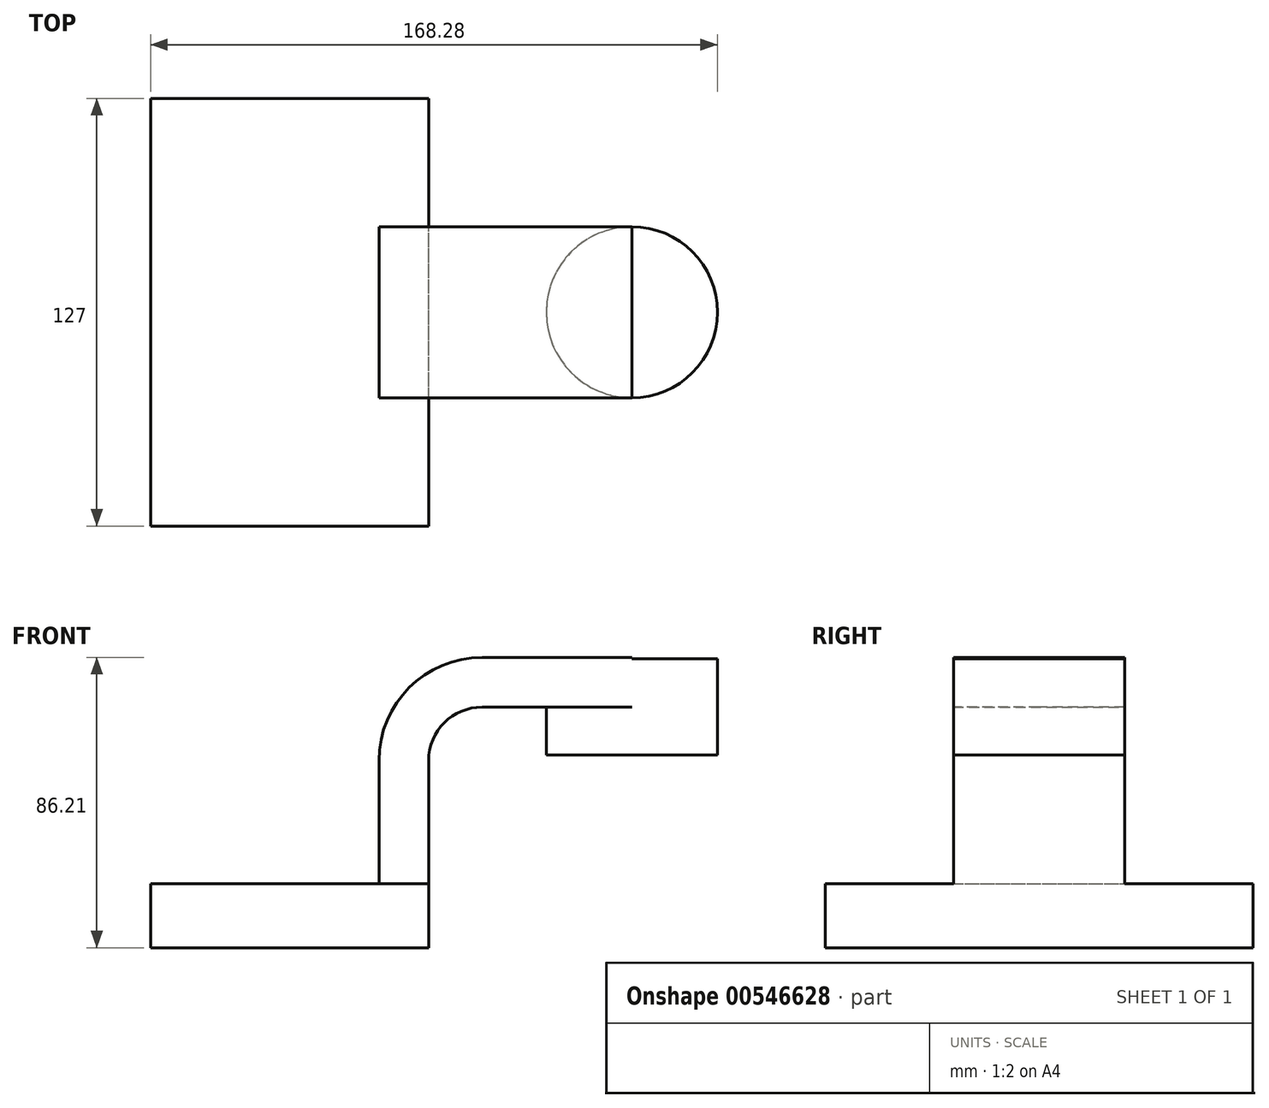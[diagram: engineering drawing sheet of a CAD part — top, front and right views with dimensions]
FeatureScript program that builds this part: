
annotation { "Feature Type Name" : "Feature", "Feature Type Description" : "" }
export const myFeature = defineFeature(function(context is Context, id is Id, definition is map)
    precondition{}
    {
        {
            var Q0;
            Q0=qCreatedBy(makeId("Front.planeOp"),FACE);
            var sketch = newSketch(context, id + "F0", { "sketchPlane" : qUnion([Q0])});
            skLineSegment(sketch, "E0.bottom", {"start": v(41.27, 9.53) * mm, "end": v(-41.28, 9.53) * mm});
            skLineSegment(sketch, "E0.top", {"start": v(41.28, -9.52) * mm, "end": v(-41.27, -9.53) * mm});
            skLineSegment(sketch, "E0.left", {"start": v(41.28, 9.53) * mm, "end": v(41.28, -9.52) * mm});
            skLineSegment(sketch, "E0.right", {"start": v(-41.28, 9.53) * mm, "end": v(-41.27, -9.52) * mm});
            skPoint(sketch, "E0.middle", {"position": v(0, 0) * mm});
            skLineSegment(sketch, "E1.bottom", {"start": v(76.2, 47.64) * mm, "end": v(76.2, 76.21) * mm});
            skLineSegment(sketch, "E1.top", {"start": v(127, 47.64) * mm, "end": v(127, 76.21) * mm});
            skLineSegment(sketch, "E1.left", {"start": v(76.2, 47.64) * mm, "end": v(127, 47.64) * mm});
            skLineSegment(sketch, "E1.right", {"start": v(76.2, 76.21) * mm, "end": v(127, 76.21) * mm});
            skPoint(sketch, "E1.middle", {"position": v(101.6, 61.93) * mm});
            skLineSegment(sketch, "E2", {"start": v(41.27, 9.53) * mm, "end": v(41.27, 46.05) * mm});
            skArc(sketch, "E3", {"start": v(41.27, 46.05) * mm, "mid": v(45.92, 57.28) * mm, "end": v(57.15, 61.93) * mm});
            skLineSegment(sketch, "E4", {"start": v(57.15, 61.93) * mm, "end": v(101.6, 61.93) * mm});
            skLineSegment(sketch, "E5.0", {"start": v(57.15, 76.68) * mm, "end": v(101.6, 76.68) * mm});
            skArc(sketch, "E5.1", {"start": v(26.52, 46.05) * mm, "mid": v(35.5, 67.7) * mm, "end": v(57.15, 76.68) * mm});
            skLineSegment(sketch, "E5.2", {"start": v(26.52, 9.53) * mm, "end": v(26.52, 46.05) * mm});
            skLineSegment(sketch, "E6", {"start": v(101.6, 47.64) * mm, "end": v(101.6, 76.68) * mm});
            skFitSpline(sketch, "E7", {"points": [v(-41.28, 9.53) * mm, v(57.15, 76.68) * mm], "startDerivative": vector(38.55, 103.6) * mm, "endDerivative": vector(184.04, -4.2) * mm});
            skSolve(sketch);
        }
        {
            var Q0;
            Q0=makeQuery(id+"F0.imprint","IMPRINT",FACE,{"disambiguationData":[TD([[makeQuery(id+"F0.imprint","IMPRINT",EDGE,{"derivedFrom":sQuery(id+"F0.wireOp",EDGE,"E0.top")}),-1.0]])]});
            extrude(context, id + "F1", {"entities" : qUnion([Q0]), "endBound" : BoundingType.SYMMETRIC, "depth" : 127 * mm, "offsetDistance" : 25.4 * mm});
        }
        {
            var Q0;
            {var subQ0=sQuery(id+"F0.wireOp",EDGE,"E2");Q0=makeQuery(id+"F0.imprint","IMPRINT",FACE,{"disambiguationData":[TD([[makeQuery(id+"F0.imprint","IMPRINT",EDGE,{"derivedFrom":subQ0}),1.0]])]});}
            var Q1;
            {var subQ0=sQuery(id+"F0.wireOp",EDGE,"E1.right");var subQ1=sQuery(id+"F0.wireOp",EDGE,"E1.bottom");var subQ2=makeQuery(id+"F0.imprint","INTERSECT",VERTEX,{"derivedFrom":[subQ1,subQ0]});Q1=makeQuery(id+"F0.imprint","IMPRINT",FACE,{"disambiguationData":[TD([[makeQuery(id+"F0.imprint","IMPRINT",EDGE,{"disambiguationData":[TD([[subQ2,1.0]])],"derivedFrom":subQ1}),-1.0]])]});}
            extrude(context, id + "F2", {"entities" : qUnion([Q0, Q1]), "operationType" : NewBodyOperationType.ADD, "endBound" : BoundingType.SYMMETRIC, "depth" : 50.8 * mm, "offsetDistance" : 25.4 * mm});
        }
        {
            var Q0;
            Q0=makeQuery(id+"F0.imprint","IMPRINT",FACE,{"disambiguationData":[TD([[makeQuery(id+"F0.imprint","IMPRINT",EDGE,{"derivedFrom":sQuery(id+"F0.wireOp",EDGE,"E5.1")}),1.0]])]});
            extrude(context, id + "F3", {"entities" : qUnion([Q0]), "operationType" : NewBodyOperationType.ADD, "endBound" : BoundingType.SYMMETRIC, "depth" : 15.88 * mm, "offsetDistance" : 25.4 * mm});
        }
        {
            var Q0;
            {var subQ1=sQuery(id+"F0.wireOp",EDGE,"E1.top");Q0=makeQuery(id+"F0.imprint","IMPRINT",FACE,{"disambiguationData":[TD([[makeQuery(id+"F0.imprint","IMPRINT",EDGE,{"derivedFrom":subQ1}),1.0]])]});}
            var Q1;
            Q1=sQuery(id+"F0.wireOp",EDGE,"E6");
            revolve(context, id + "F4", {"operationType" : NewBodyOperationType.ADD, "entities" : qUnion([Q0]), "axis" : qUnion([Q1]), "revolveType" : RevolveType.FULL});
        }
    });
